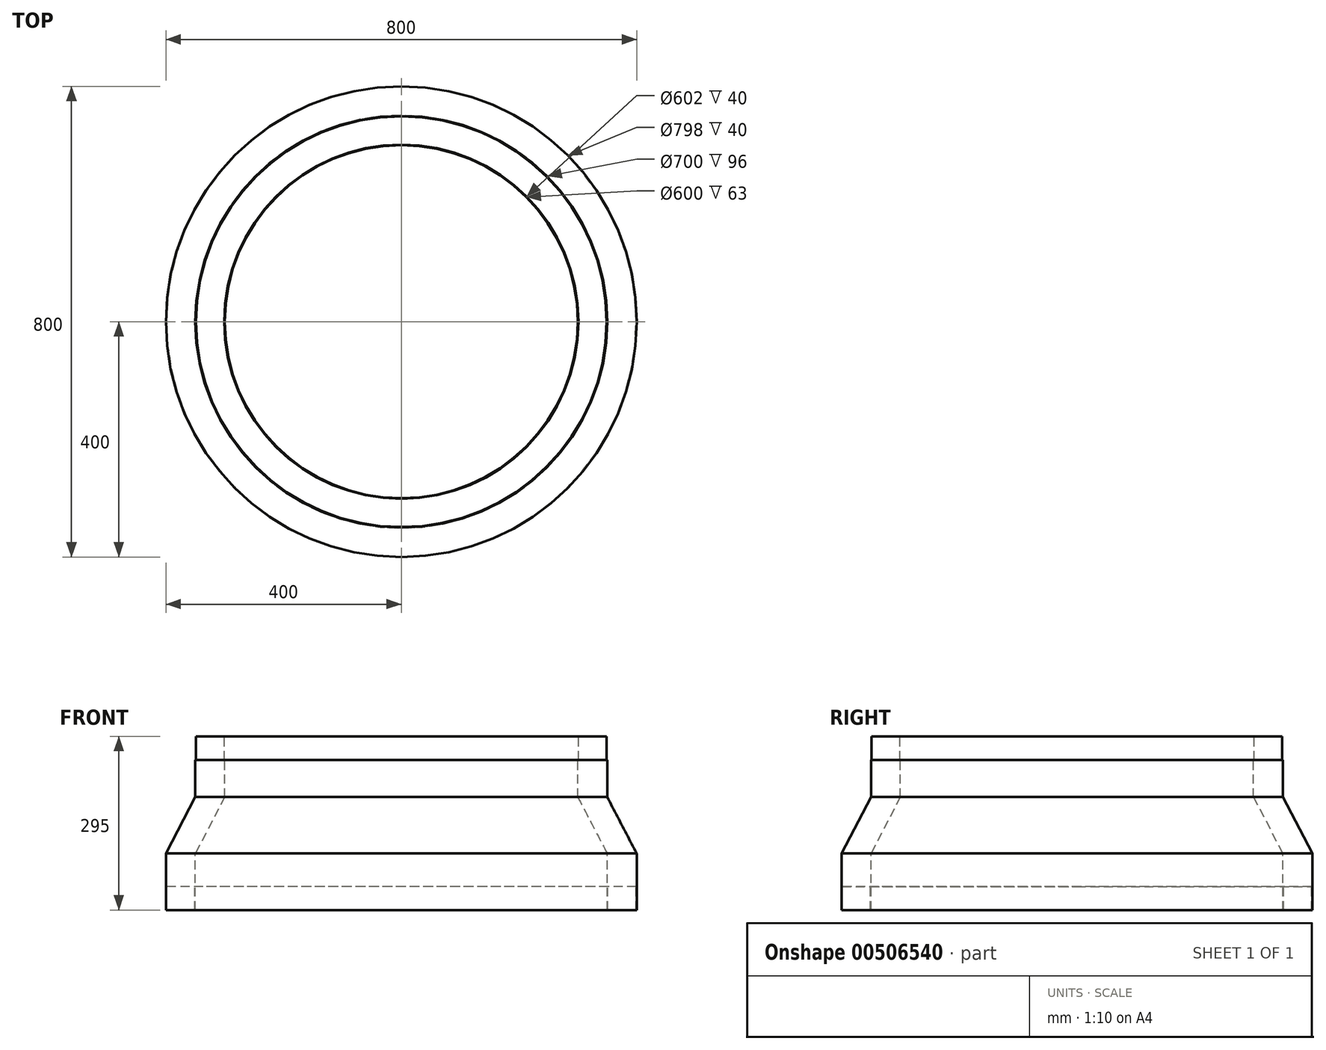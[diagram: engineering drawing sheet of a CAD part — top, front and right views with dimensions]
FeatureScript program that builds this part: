
annotation { "Feature Type Name" : "Feature", "Feature Type Description" : "" }
export const myFeature = defineFeature(function(context is Context, id is Id, definition is map)
    precondition{}
    {
        {
            var Q0;
            Q0=qCreatedBy(makeId("Front.planeOp"),FACE);
            var sketch = newSketch(context, id + "F0", { "sketchPlane" : qUnion([Q0])});
            skLineSegment(sketch, "E0", {"start": v(0, 433.08) * mm, "end": v(0, -434.74) * mm, "construction": true});
            skLineSegment(sketch, "E1", {"start": v(-350, -258.87) * mm, "end": v(-350, -162.87) * mm});
            skLineSegment(sketch, "E2", {"start": v(-350, -258.87) * mm, "end": v(-351, -258.87) * mm});
            skLineSegment(sketch, "E3", {"start": v(-351, -258.87) * mm, "end": v(-351, -218.87) * mm});
            skLineSegment(sketch, "E4", {"start": v(-351, -218.87) * mm, "end": v(-399, -218.87) * mm});
            skLineSegment(sketch, "E5", {"start": v(-399, -218.87) * mm, "end": v(-399, -258.87) * mm});
            skLineSegment(sketch, "E6", {"start": v(-399, -258.87) * mm, "end": v(-400, -258.87) * mm});
            skLineSegment(sketch, "E7", {"start": v(-400, -258.87) * mm, "end": v(-400, -162.87) * mm});
            skLineSegment(sketch, "E8", {"start": v(-349, 36.13) * mm, "end": v(-301, 36.13) * mm});
            skLineSegment(sketch, "E9", {"start": v(-301, 36.13) * mm, "end": v(-301, -3.87) * mm});
            skLineSegment(sketch, "E10", {"start": v(-301, -3.87) * mm, "end": v(-300, -3.87) * mm});
            skLineSegment(sketch, "E11", {"start": v(-300, -3.87) * mm, "end": v(-300, -66.87) * mm});
            skLineSegment(sketch, "E12", {"start": v(-349, 36.13) * mm, "end": v(-349, -3.87) * mm});
            skLineSegment(sketch, "E13", {"start": v(-349, -3.87) * mm, "end": v(-350, -3.87) * mm});
            skLineSegment(sketch, "E14", {"start": v(-350, -3.87) * mm, "end": v(-350, -66.87) * mm});
            skLineSegment(sketch, "E15", {"start": v(-300, -66.87) * mm, "end": v(-350, -162.87) * mm});
            skLineSegment(sketch, "E16", {"start": v(-350, -66.87) * mm, "end": v(-400, -162.87) * mm});
            skSolve(sketch);
        }
        {
            var Q0;
            Q0=qSketchRegion(id+"F0",true);
            var Q1;
            Q1=sQuery(id+"F0.wireOp",EDGE,"E0");
            revolve(context, id + "F1", {"entities" : qUnion([Q0]), "axis" : qUnion([Q1]), "revolveType" : RevolveType.FULL});
        }
    });
